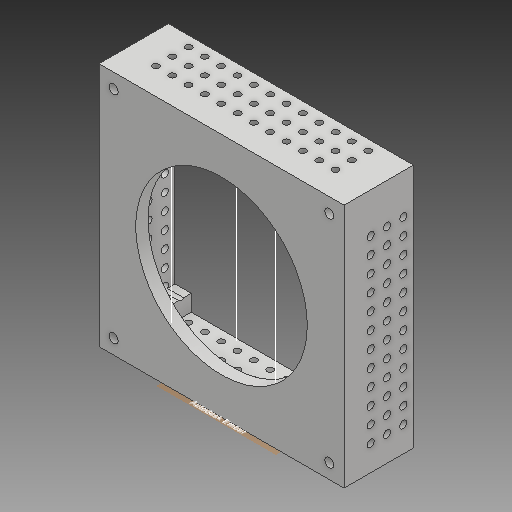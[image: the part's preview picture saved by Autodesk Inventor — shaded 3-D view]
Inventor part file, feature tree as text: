
AUTODESK INVENTOR PART (.ipt)
format: ipt  version: 2018 (Build 220112000, 112)  size: 484,352 bytes
history: native  units: mm
features: sketch x6, extrude x4, pattern_linear x2
ambient origin geometry x8: Origin, YZ Plane, XZ Plane, XY Plane, X Axis, Y Axis, Z Axis, Center Point
bodies: Solid1 (feature_tree)
feature tree (12):
  sketch  "Sketch1"  dims[d0=150.0mm d1=150.0mm]
  extrude  "Extrusion1"  Depth=150.0mm
  extrude  "Extrusion3"  Depth=4.0mm
  extrude  "Extrusion4"  Depth=10.0mm
  pattern_linear  "Rectangular Pattern1"  Count1=2 Spacing1=132.0mm
  extrude  "Extrusion5"  Depth=132.0mm
  pattern_linear  "Rectangular Pattern2"  Count1=8 Spacing1=0.0mm
  sketch  "Sketch9"  dims[d17=20.0mm d19=132.0mm d20=5.5mm d21=80.0mm d22=0.0mm d23=20.0mm d25=132.0mm d26=20.0mm d28=132.0mm]
  sketch  "Sketch2"  dims[d2=7.5mm d3=0.0mm d7=4.0mm]
  sketch  "Sketch4"  dims[d8=35.0mm d9=0.0mm d10=10.0mm]
  sketch  "Sketch5"  dims[d11=10.0mm]
  sketch  "Sketch6"  dims[d12=35.0mm d13=0.0mm d14=20.0mm d16=132.0mm]
